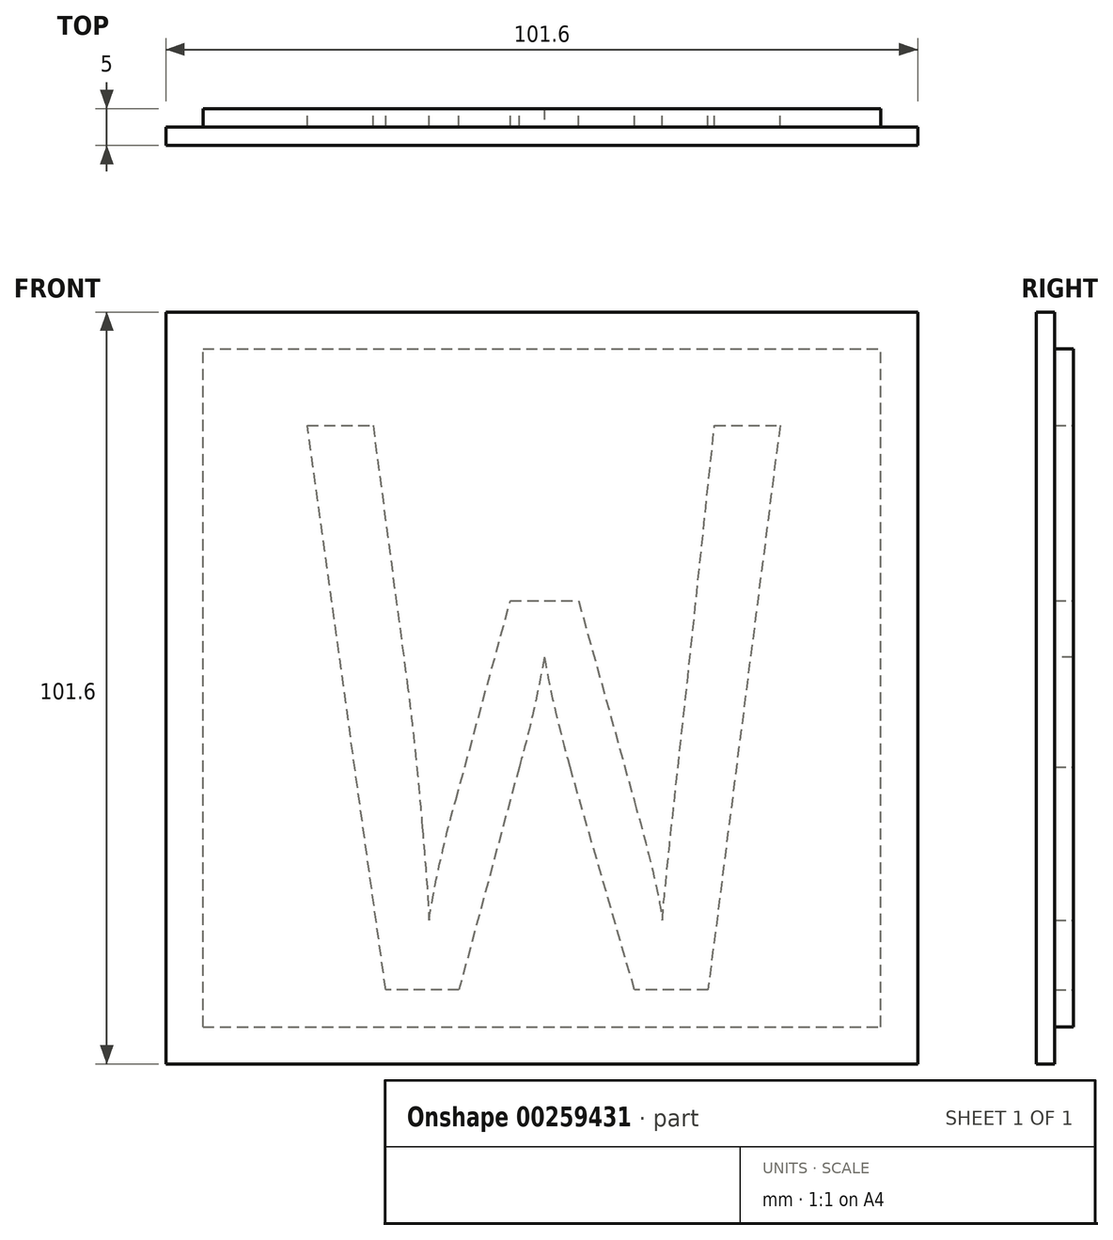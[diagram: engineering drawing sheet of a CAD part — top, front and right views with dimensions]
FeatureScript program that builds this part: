
annotation { "Feature Type Name" : "Feature", "Feature Type Description" : "" }
export const myFeature = defineFeature(function(context is Context, id is Id, definition is map)
    precondition{}
    {
        {
            var Q0;
            Q0=qCreatedBy(makeId("Front.planeOp"),FACE);
            var sketch = newSketch(context, id + "F0", { "sketchPlane" : qUnion([Q0])});
            skLineSegment(sketch, "E0.bottom", {"start": v(0, 0) * mm, "end": v(101.6, 0) * mm});
            skLineSegment(sketch, "E0.top", {"start": v(0, 101.6) * mm, "end": v(101.6, 101.6) * mm});
            skLineSegment(sketch, "E0.left", {"start": v(0, 0) * mm, "end": v(0, 101.6) * mm});
            skLineSegment(sketch, "E0.right", {"start": v(101.6, 0) * mm, "end": v(101.6, 101.6) * mm});
            skLineSegment(sketch, "E1.0", {"start": v(5, 5) * mm, "end": v(5, 96.6) * mm});
            skLineSegment(sketch, "E1.1", {"start": v(5, 5) * mm, "end": v(96.6, 5) * mm});
            skLineSegment(sketch, "E1.2", {"start": v(96.6, 5) * mm, "end": v(96.6, 96.6) * mm});
            skLineSegment(sketch, "E1.3", {"start": v(5, 96.6) * mm, "end": v(96.6, 96.6) * mm});
            skSolve(sketch);
        }
        {
            var Q0;
            Q0=makeQuery(id+"F0.imprint","IMPRINT",FACE,{"disambiguationData":[TD([[makeQuery(id+"F0.imprint","IMPRINT",EDGE,{"derivedFrom":sQuery(id+"F0.wireOp",EDGE,"E0.bottom")}),1.0]])]});
            var Q1;
            Q1=makeQuery(id+"F0.imprint","IMPRINT",FACE,{"disambiguationData":[TD([[makeQuery(id+"F0.imprint","IMPRINT",EDGE,{"derivedFrom":sQuery(id+"F0.wireOp",EDGE,"E1.0")}),-1.0]])]});
            extrude(context, id + "F1", {"entities" : qUnion([Q0, Q1]), "depth" : 5 * mm, "offsetDistance" : 25 * mm});
        }
        {
            var Q0;
            Q0=makeQuery(id+"F0.imprint","IMPRINT",FACE,{"disambiguationData":[TD([[makeQuery(id+"F0.imprint","IMPRINT",EDGE,{"derivedFrom":sQuery(id+"F0.wireOp",EDGE,"E0.bottom")}),1.0]])]});
            extrude(context, id + "F2", {"entities" : qUnion([Q0]), "operationType" : NewBodyOperationType.REMOVE, "depth" : 2.5 * mm, "offsetDistance" : 25 * mm});
        }
        {
            var Q0;
            Q0=makeQuery(id+"F0.imprint","IMPRINT",FACE,{"disambiguationData":[TD([[makeQuery(id+"F0.imprint","IMPRINT",EDGE,{"derivedFrom":sQuery(id+"F0.wireOp",EDGE,"E1.0")}),-1.0]])]});
            var sketch = newSketch(context, id + "F3", { "sketchPlane" : qUnion([Q0])});
            skLineSegment(sketch, "E2", {"start": v(0, 0) * mm, "end": v(59, 0) * mm, "construction": true});
            skLineSegment(sketch, "E3", {"start": v(59, 0) * mm, "end": v(59, 10) * mm, "construction": true});
            skLineSegment(sketch, "E4", {"start": v(59, 10) * mm, "end": v(99, 10) * mm, "construction": true});
            skLineSegment(sketch, "E5", {"start": v(99, 10) * mm, "end": v(99, 86.9) * mm, "construction": true});
            skLineSegment(sketch, "E6", {"start": v(99, 86.9) * mm, "end": v(19, 86.9) * mm, "construction": true});
            skText(sketch, "E7", { "text": "W", "fontName": "DroidSansMono.ttf"});
            skLineSegment(sketch, "E8", {"start": v(0, 0) * mm, "end": v(50.8, 0) * mm, "construction": true});
            skLineSegment(sketch, "E9", {"start": v(50.8, 0) * mm, "end": v(50.8, 101.68) * mm, "construction": true});
            const initialGuessF3  = {"E7": [0.019, 0.01, 1, 0, 0.0769]};
            skSetInitialGuess(sketch, initialGuessF3);
            skSolve(sketch);
        }
        {
            var Q0;
            Q0=makeQuery(id+"F3.imprint","IMPRINT",FACE,{"disambiguationData":[TD([[makeQuery(id+"F3.imprint","IMPRINT",EDGE,{"derivedFrom":sQuery(id+"F3.wireOp",EDGE,"E7.sketch_text.stroke-0")}),-1.0]])]});
            extrude(context, id + "F4", {"entities" : qUnion([Q0]), "operationType" : NewBodyOperationType.REMOVE, "depth" : 2.5 * mm, "offsetDistance" : 25 * mm});
        }
    });
